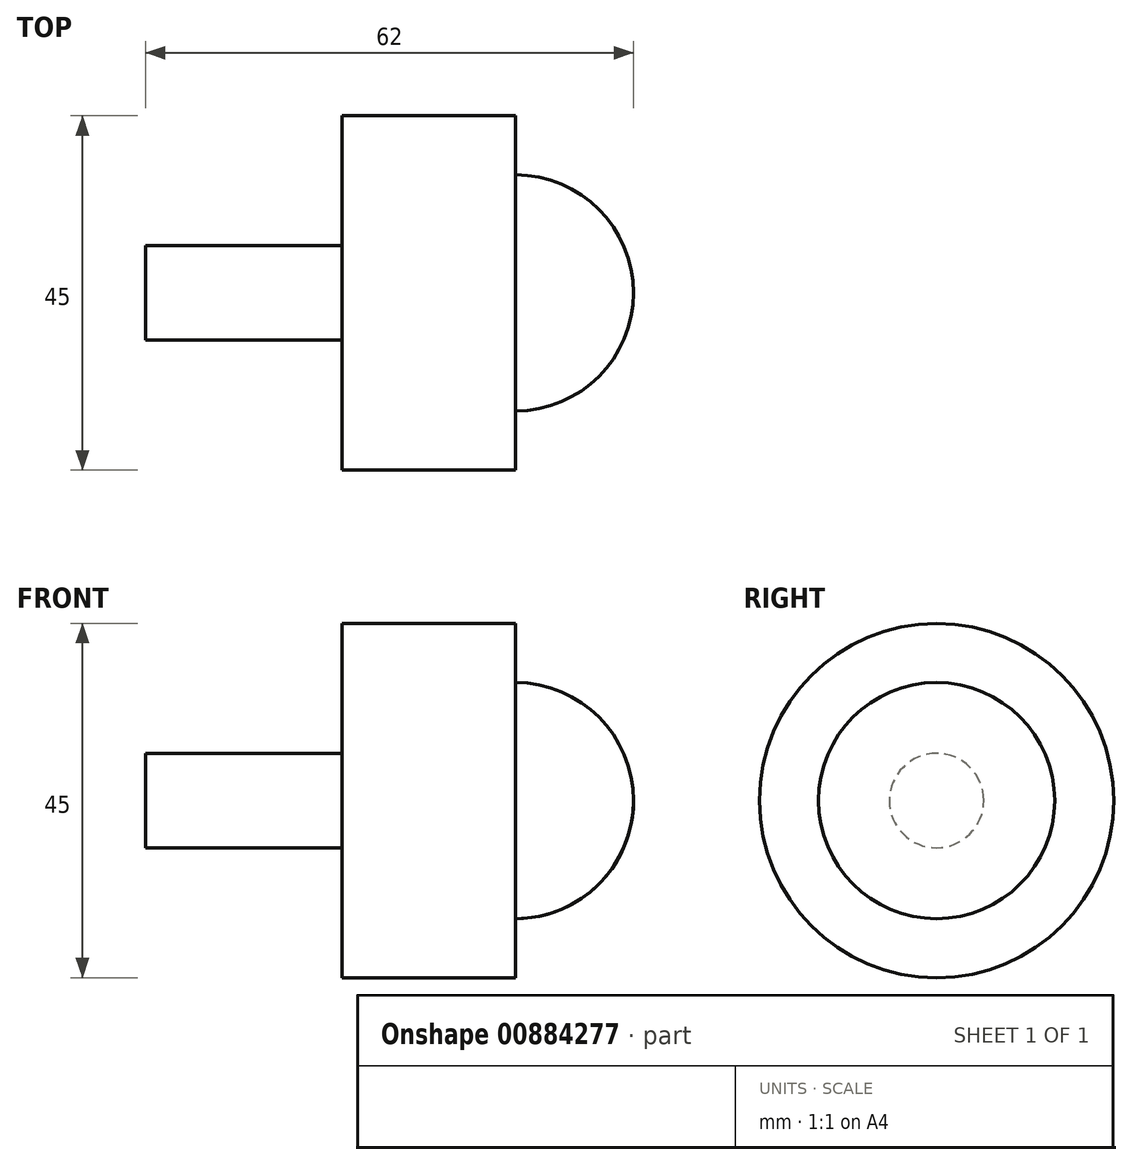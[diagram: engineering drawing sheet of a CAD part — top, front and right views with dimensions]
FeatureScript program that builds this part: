
annotation { "Feature Type Name" : "Feature", "Feature Type Description" : "" }
export const myFeature = defineFeature(function(context is Context, id is Id, definition is map)
    precondition{}
    {
        {
            var Q0;
            Q0=qCreatedBy(makeId("Front.planeOp"),FACE);
            var sketch = newSketch(context, id + "F0", { "sketchPlane" : qUnion([Q0])});
            skLineSegment(sketch, "E0", {"start": v(0, 0) * mm, "end": v(0, 6) * mm});
            skLineSegment(sketch, "E1", {"start": v(0, 6) * mm, "end": v(25, 6) * mm});
            skLineSegment(sketch, "E2", {"start": v(25, 6) * mm, "end": v(25, 22.5) * mm});
            skLineSegment(sketch, "E3", {"start": v(25, 22.5) * mm, "end": v(47, 22.5) * mm});
            skLineSegment(sketch, "E4", {"start": v(47, 22.5) * mm, "end": v(47, 15) * mm});
            skArc(sketch, "E5", {"start": v(47, 15) * mm, "mid": v(57.6, 10.6) * mm, "end": v(62, 0) * mm});
            skLineSegment(sketch, "E6", {"start": v(0, 0) * mm, "end": v(62, 0) * mm});
            skSolve(sketch);
        }
        {
            var Q0;
            Q0 = qSketchRegion(id + "F0", true);
            var Q1;
            Q1=sQuery(id+"F0.wireOp",EDGE,"E6");
            revolve(context, id + "F1", {"surfaceOperationType" : NewSurfaceOperationType.NEW, "entities" : qUnion([Q0]), "axis" : qUnion([Q1]), "revolveType" : RevolveType.FULL});
        }
    });
